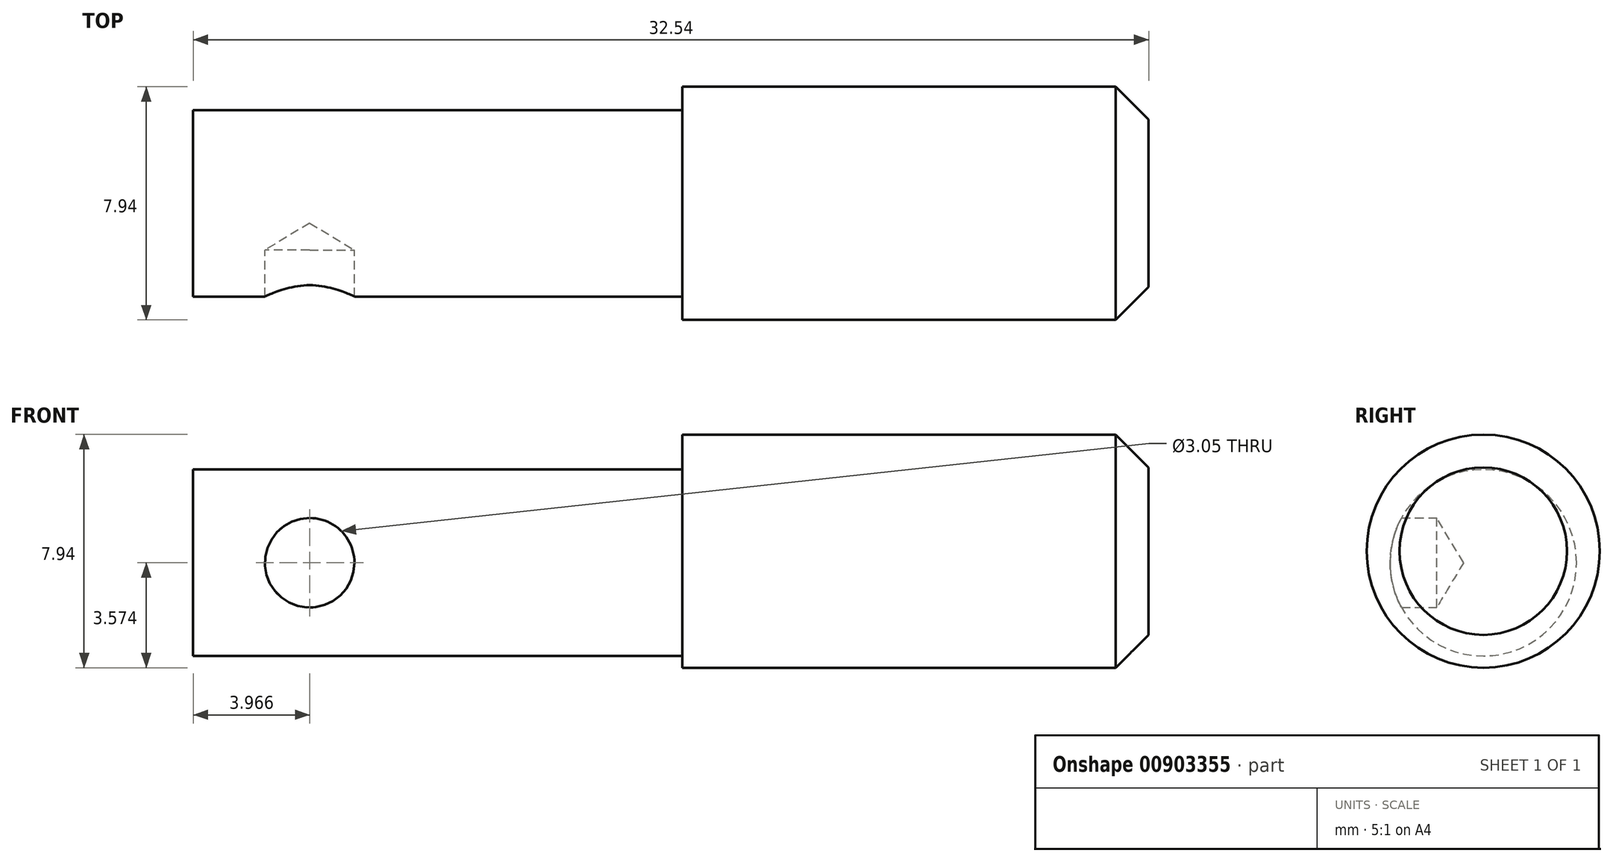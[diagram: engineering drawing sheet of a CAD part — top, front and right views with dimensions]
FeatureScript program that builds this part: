
annotation { "Feature Type Name" : "Feature", "Feature Type Description" : "" }
export const myFeature = defineFeature(function(context is Context, id is Id, definition is map)
    precondition{}
    {
        {
            var Q0;
            Q0=qCreatedBy(makeId("Right.planeOp"),FACE);
            var sketch = newSketch(context, id + "F0", { "sketchPlane" : qUnion([Q0])});
            skCircle(sketch, "E0", {"center": v(0, 0) * mm, "radius": 3.97 * mm});
            skCircle(sketch, "E1", {"center": v(0, -0.4) * mm, "radius": 3.18 * mm});
            skSolve(sketch);
        }
        {
            var Q0;
            Q0=makeQuery(id+"F0.imprint","IMPRINT",FACE,{"disambiguationData":[TD([[makeQuery(id+"F0.imprint","IMPRINT",EDGE,{"derivedFrom":sQuery(id+"F0.wireOp",EDGE,"E0")}),1.0]])]});
            var Q1;
            Q1=makeQuery(id+"F0.imprint","IMPRINT",FACE,{"disambiguationData":[TD([[makeQuery(id+"F0.imprint","IMPRINT",EDGE,{"derivedFrom":sQuery(id+"F0.wireOp",EDGE,"E1")}),1.0]])]});
            extrude(context, id + "F1", {"entities" : qUnion([Q0, Q1]), "flatOperationType" : FlatOperationType.REMOVE, "depth" : 15.88 * mm, "offsetDistance" : 25.4 * mm, "domain" : OperationDomain.MODEL});
        }
        {
            var Q0;
            Q0=makeQuery(id+"F0.imprint","IMPRINT",FACE,{"disambiguationData":[TD([[makeQuery(id+"F0.imprint","IMPRINT",EDGE,{"derivedFrom":sQuery(id+"F0.wireOp",EDGE,"E1")}),1.0]])]});
            extrude(context, id + "F2", {"entities" : qUnion([Q0]), "operationType" : NewBodyOperationType.ADD, "flatOperationType" : FlatOperationType.REMOVE, "oppositeDirection" : true, "depth" : 16.66 * mm, "offsetDistance" : 25.4 * mm, "domain" : OperationDomain.MODEL});
        }
        {
            var Q0;
            Q0=makeQuery(id+"F1.opExtrude","CAP_EDGE",EDGE,{"disambiguationData":[OSD([sQuery(id+"F0.wireOp",EDGE,"E0")])],"isStart":false});
            chamfer(context, id + "F3", {"entities" : qUnion([Q0]), "width" : 1.12 * mm, "tangentPropagation" : true});
        }
        {
            var Q0;
            Q0=qCreatedBy(makeId("Front.planeOp"),FACE);
            cPlane(context, id + "F4", {"entities" : qUnion([Q0]), "cplaneType" : CPlaneType.OFFSET, "offset" : 3.17 * mm, "width" : 152.4 * mm, "height" : 152.4 * mm});
        }
        {
            var Q0;
            Q0=qCreatedBy(id+"F4.planeOp",FACE);
            var sketch = newSketch(context, id + "F5", { "sketchPlane" : qUnion([Q0])});
            skPoint(sketch, "E2", {"position": v(-12.7, -0.4) * mm});
            skSolve(sketch);
        }
        {
            var Q0;
            Q0=sQuery(id+"F5.wireOp",VERTEX,"E2");
            var Q1;
            Q1=makeQuery(id+"F1.opExtrude","SWEPT_BODY",BODY,{"disambiguationData":[OSD([sQuery(id+"F0.wireOp",EDGE,"E0")])]});
            hole(context, id + "F6", {"style" : HoleStyle.SIMPLE, "endStyle" : HoleEndStyle.BLIND, "standardTappedOrClearance" : lookupTablePath({ "fit" : "Close (ASME)", "standard" : "ANSI", "size" : "#4", "type" : "Clearance" }), "standardBlindInLast" : lookupTablePath({ "fit" : "Close", "standard" : "ANSI", "size" : "#4", "type" : "Clearance" }), "holeDiameter" : 3.05 * mm, "majorDiameter" : 6.35 * mm, "holeDepth" : 1.59 * mm, "tappedDepth" : 14.33 * mm, "tapClearance" : 3, "locations" : qUnion([Q0]), "scope" : qUnion([Q1]), "startStyle" : HoleStartStyle.SKETCH});
        }
    });
